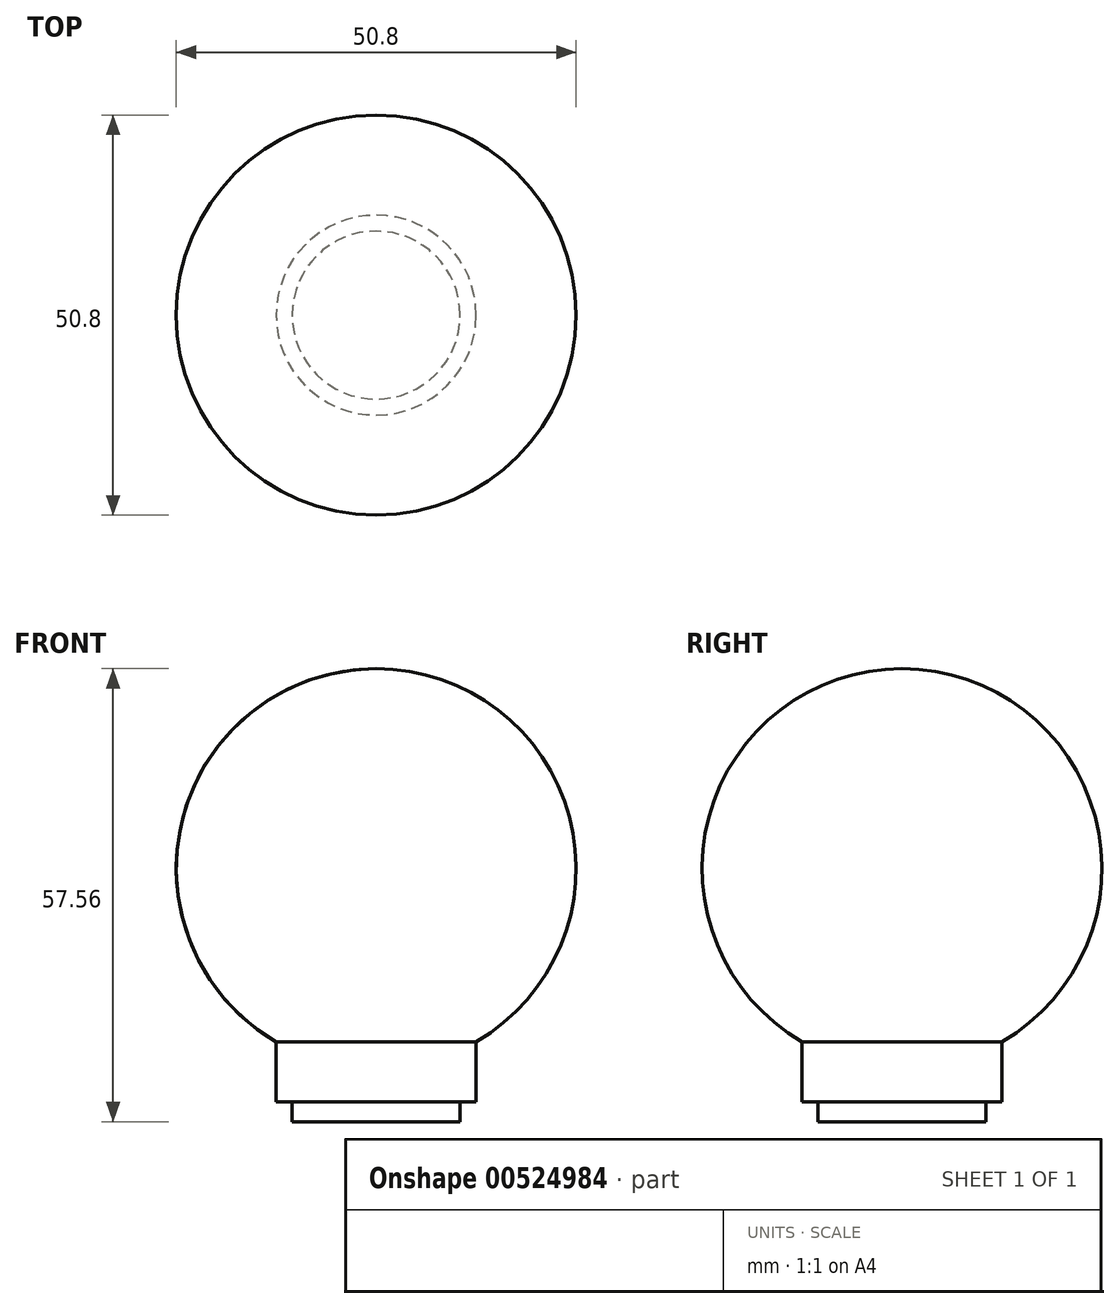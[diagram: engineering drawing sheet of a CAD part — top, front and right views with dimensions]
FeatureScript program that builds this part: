
annotation { "Feature Type Name" : "Feature", "Feature Type Description" : "" }
export const myFeature = defineFeature(function(context is Context, id is Id, definition is map)
    precondition{}
    {
        {
            var Q0;
            Q0=qCreatedBy(makeId("Front.planeOp"),FACE);
            var sketch = newSketch(context, id + "F0", { "sketchPlane" : qUnion([Q0])});
            skLineSegment(sketch, "E0", {"start": v(0, 0) * mm, "end": v(-10.67, 0) * mm});
            skLineSegment(sketch, "E1", {"start": v(-12.7, 2.54) * mm, "end": v(-12.7, 10.16) * mm});
            skLineSegment(sketch, "E2", {"start": v(-12.7, 10.16) * mm, "end": v(0, 10.16) * mm, "construction": true});
            skLineSegment(sketch, "E3", {"start": v(0, 10.16) * mm, "end": v(0, 0) * mm, "construction": true});
            skArc(sketch, "E4", {"start": v(0, 57.56) * mm, "mid": v(-24.53, 38.73) * mm, "end": v(-12.7, 10.16) * mm});
            skLineSegment(sketch, "E5", {"start": v(0, 57.56) * mm, "end": v(0, 0) * mm});
            skLineSegment(sketch, "E6", {"start": v(-10.67, 0) * mm, "end": v(-10.67, 2.54) * mm});
            skLineSegment(sketch, "E7", {"start": v(-10.67, 2.54) * mm, "end": v(-12.7, 2.54) * mm});
            skSolve(sketch);
        }
        {
            var Q0;
            Q0=sQuery(id+"F0.wireOp",EDGE,"E4");
            var Q1;
            Q1=sQuery(id+"F0.wireOp",EDGE,"E1");
            var Q2;
            Q2=sQuery(id+"F0.wireOp",EDGE,"E0");
            var Q3;
            Q3=sQuery(id+"F0.wireOp",EDGE,"E6");
            var Q4;
            Q4=sQuery(id+"F0.wireOp",EDGE,"E7");
            var Q5;
            Q5=sQuery(id+"F0.wireOp",EDGE,"E5");
            revolve(context, id + "F1", {"bodyType" : ToolBodyType.SURFACE, "surfaceEntities" : qUnion([Q0, Q1, Q2, Q3, Q4]), "axis" : qUnion([Q5]), "revolveType" : RevolveType.FULL});
        }
    });
